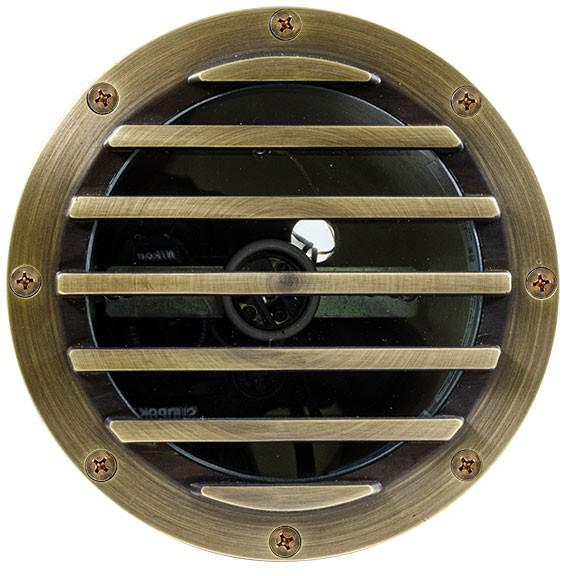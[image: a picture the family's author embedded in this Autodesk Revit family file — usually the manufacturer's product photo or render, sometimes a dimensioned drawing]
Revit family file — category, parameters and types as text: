
# Revit family: Alcon-9038-Revit-Family
name_source: partatom
category: Luminarias
units: mm (PartAtom-declared; Revit-internal decimal feet)

## family parameters
Anfitrión = Cara
Compartido = No
Corte con vacíos al cargar = No
Cota de conector redondo = Usar diámetro
Mantener orientación de anotación = No
Origen de luz = Sí
Punto de cálculo de habitación = No
Tipo de pieza = Normal

## types (1)
- Alcon-9038-Revit-Family
    Cambio de temperatura de color de luz atenuada = <Ninguno>
    Elevación por defecto = 4' - 0"
    Fabricante = Alcon Lighting
    Filtro de color = 16777215
    GLASS LENS = Analytical Panels
    HOUSING = <Por categoría>
    LENS GLASS = Glass
    Link to IES File = https://www.alconlighting.com
    Longitud de símbolo de origen de luz = 10' - 0"
    Modelo = Alcon Lighting 9038
    Product Data URL = https://www.alconlighting.com
    Product Page = https://www.alconlighting.com
    TAP LENS = <Por categoría>
    TOP FINISH = <Por categoría>
    URL = https://www.alconlighting.com
    Ángulo de campo de foco = 90.00°
    Ángulo de enfoque = 30.00°
    Ángulo de inclinación = 60.00°

## geometry (parser evidence)
native form markers: Sweep x2
no freeform markers — native parametric forms only
